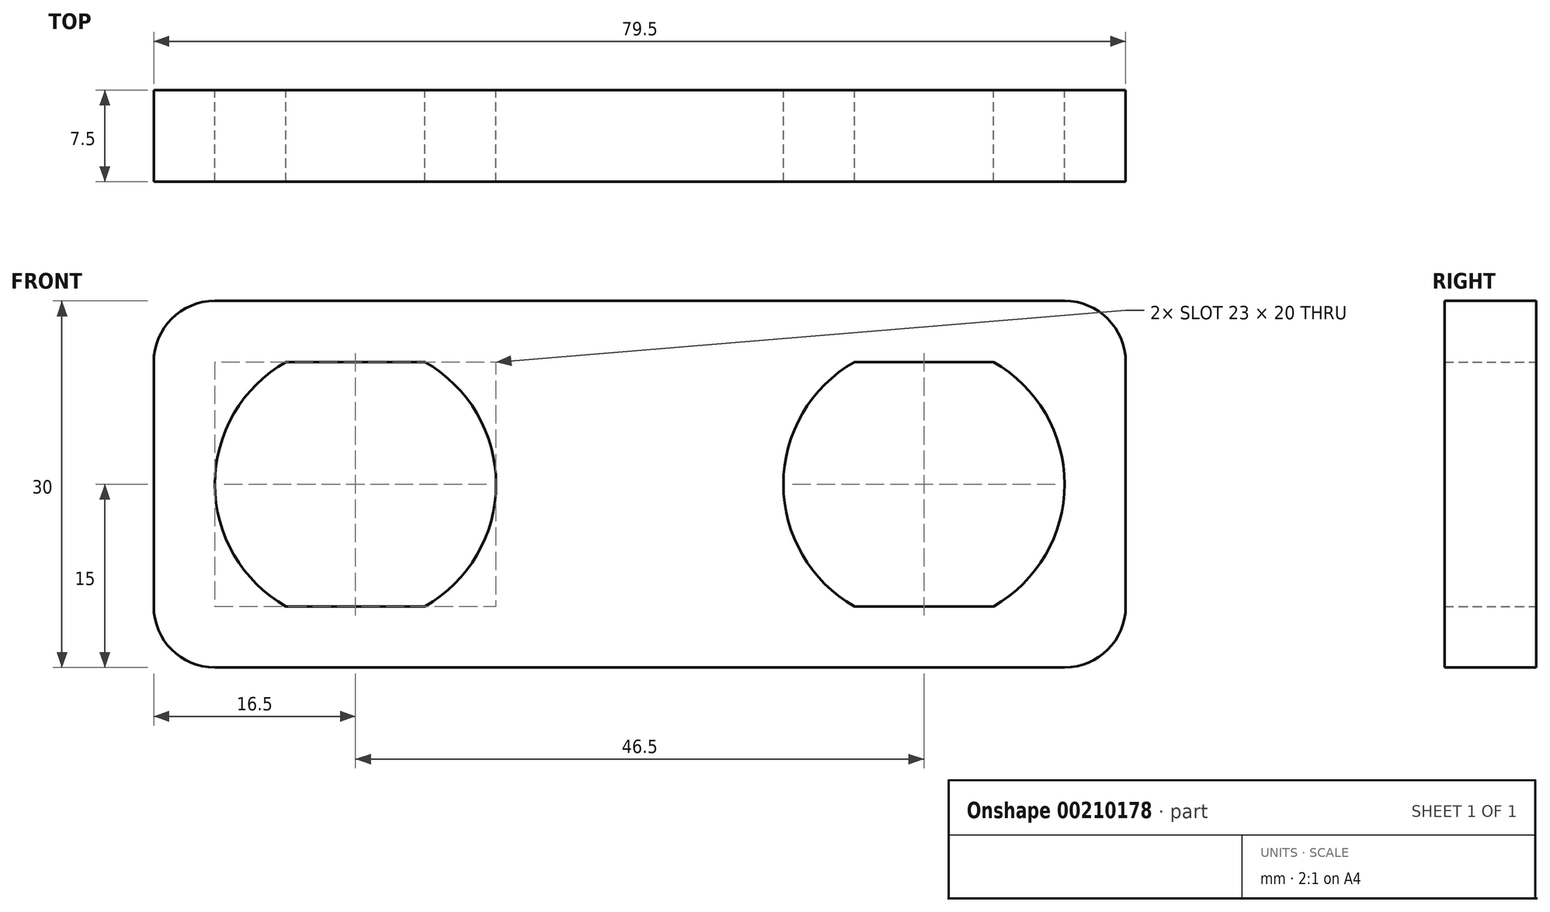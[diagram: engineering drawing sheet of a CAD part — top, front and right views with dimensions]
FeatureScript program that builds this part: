
annotation { "Feature Type Name" : "Feature", "Feature Type Description" : "" }
export const myFeature = defineFeature(function(context is Context, id is Id, definition is map)
    precondition{}
    {
        {
            var Q0;
            Q0=qCreatedBy(makeId("Front.planeOp"),FACE);
            var sketch = newSketch(context, id + "F0", { "sketchPlane" : qUnion([Q0])});
            skLineSegment(sketch, "E0", {"start": v(0, 0) * mm, "end": v(-46.5, 0) * mm});
            skCircle(sketch, "E1", {"center": v(-46.5, 0) * mm, "radius": 11.5 * mm});
            skCircle(sketch, "E2", {"center": v(0, 0) * mm, "radius": 11.5 * mm});
            skLineSegment(sketch, "E3", {"start": v(-35, 0) * mm, "end": v(-11.5, 0) * mm});
            skLineSegment(sketch, "E4", {"start": v(-46.5, 0) * mm, "end": v(-46.5, 10) * mm});
            skLineSegment(sketch, "E5", {"start": v(-46.5, 0) * mm, "end": v(-46.5, -10) * mm});
            skLineSegment(sketch, "E6", {"start": v(-46.5, 10) * mm, "end": v(-40.82, 10) * mm});
            skLineSegment(sketch, "E7", {"start": v(5.68, -10) * mm, "end": v(-5.68, -10) * mm});
            skLineSegment(sketch, "E8.trimOffspring", {"start": v(-5.68, 10) * mm, "end": v(5.68, 10) * mm});
            skLineSegment(sketch, "E9.trimOffspring", {"start": v(-40.82, -10) * mm, "end": v(-52.18, -10) * mm});
            skLineSegment(sketch, "E10", {"start": v(-46.5, 10) * mm, "end": v(-52.18, 10) * mm});
            skLineSegment(sketch, "E11", {"start": v(-58, 0) * mm, "end": v(-63, 0) * mm});
            skLineSegment(sketch, "E12", {"start": v(-63, 0) * mm, "end": v(-63, 15) * mm});
            skLineSegment(sketch, "E13", {"start": v(11.5, 0) * mm, "end": v(16.5, 0) * mm});
            skLineSegment(sketch, "E14", {"start": v(16.5, 0) * mm, "end": v(16.5, 15) * mm});
            skLineSegment(sketch, "E15", {"start": v(16.5, 15) * mm, "end": v(-63, 15) * mm});
            skLineSegment(sketch, "E16.MirrorCS", {"start": v(16.5, 0) * mm, "end": v(16.5, -15) * mm});
            skLineSegment(sketch, "E17.MirrorCS", {"start": v(16.5, -15) * mm, "end": v(-63, -15) * mm});
            skLineSegment(sketch, "E18.MirrorCS", {"start": v(-63, 0) * mm, "end": v(-63, -15) * mm});
            skText(sketch, "E19", { "text": "259", "fontName": "OpenSans-Regular.ttf"});
            const initialGuessF0  = {"E19": [-0.03467, 0.00376, 1, 0, 0.0096]};
            skSetInitialGuess(sketch, initialGuessF0);
            skSolve(sketch);
        }
        {
            var Q0;
            Q0 = qSketchRegion(id + "F0", true);
            var Q1;
            Q1=makeQuery(id+"F0.imprint","IMPRINT",FACE,{"disambiguationData":[TD([[makeQuery(id+"F0.imprint","IMPRINT",EDGE,{"derivedFrom":sQuery(id+"F0.wireOp",EDGE,"E19.sketch_text.stroke-55")}),1.0]])]});
            var Q2;
            Q2=makeQuery(id+"F0.imprint","IMPRINT",FACE,{"disambiguationData":[TD([[makeQuery(id+"F0.imprint","IMPRINT",EDGE,{"derivedFrom":sQuery(id+"F0.wireOp",EDGE,"E19.sketch_text.stroke-39")}),-1.0]])]});
            var Q3;
            Q3=makeQuery(id+"F0.imprint","IMPRINT",FACE,{"disambiguationData":[TD([[makeQuery(id+"F0.imprint","IMPRINT",EDGE,{"derivedFrom":sQuery(id+"F0.wireOp",EDGE,"E19.sketch_text.stroke-20")}),-1.0]])]});
            var Q4;
            Q4=makeQuery(id+"F0.imprint","IMPRINT",FACE,{"disambiguationData":[TD([[makeQuery(id+"F0.imprint","IMPRINT",EDGE,{"derivedFrom":sQuery(id+"F0.wireOp",EDGE,"E19.sketch_text.stroke-0")}),-1.0]])]});
            var Q5;
            {var subQ0=sQuery(id+"F0.wireOp",EDGE,"E8.trimOffspring");Q5=makeQuery(id+"F0.imprint","IMPRINT",FACE,{"disambiguationData":[TD([[makeQuery(id+"F0.imprint","IMPRINT",EDGE,{"derivedFrom":subQ0}),1.0]])]});}
            var Q6;
            {var subQ0=sQuery(id+"F0.wireOp",EDGE,"E7");Q6=makeQuery(id+"F0.imprint","IMPRINT",FACE,{"disambiguationData":[TD([[makeQuery(id+"F0.imprint","IMPRINT",EDGE,{"derivedFrom":subQ0}),1.0]])]});}
            var Q7;
            {var subQ0=sQuery(id+"F0.wireOp",EDGE,"E9.trimOffspring");var subQ1=sQuery(id+"F0.wireOp",EDGE,"E1");var subQ2=makeQuery(id+"F0.imprint","INTERSECT",VERTEX,{"disambiguationData":[OD(0.0)],"derivedFrom":[subQ1,subQ0]});Q7=makeQuery(id+"F0.imprint","IMPRINT",FACE,{"disambiguationData":[TD([[makeQuery(id+"F0.imprint","IMPRINT",EDGE,{"disambiguationData":[TD([[subQ2,1.0]])],"derivedFrom":subQ1}),1.0]])]});}
            var Q8;
            {var subQ0=sQuery(id+"F0.wireOp",EDGE,"E6");Q8=makeQuery(id+"F0.imprint","IMPRINT",FACE,{"disambiguationData":[TD([[makeQuery(id+"F0.imprint","IMPRINT",EDGE,{"derivedFrom":subQ0}),1.0]])]});}
            extrude(context, id + "F1", {"entities" : qUnion([Q0, Q1, Q2, Q3, Q4, Q5, Q6, Q7, Q8]), "depth" : 7.5 * mm});
        }
        {
            var Q0;
            Q0=makeQuery(id+"F1.opExtrude","SWEPT_EDGE",EDGE,{"disambiguationData":[OSD([sQuery(id+"F0.wireOp",EDGE,"E17.MirrorCS"),sQuery(id+"F0.wireOp",EDGE,"E18.MirrorCS")])]});
            var Q1;
            Q1=makeQuery(id+"F1.opExtrude","SWEPT_EDGE",EDGE,{"disambiguationData":[OSD([sQuery(id+"F0.wireOp",EDGE,"E12"),sQuery(id+"F0.wireOp",EDGE,"E15")])]});
            var Q2;
            Q2=makeQuery(id+"F1.opExtrude","SWEPT_EDGE",EDGE,{"disambiguationData":[OSD([sQuery(id+"F0.wireOp",EDGE,"E16.MirrorCS"),sQuery(id+"F0.wireOp",EDGE,"E17.MirrorCS")])]});
            var Q3;
            Q3=makeQuery(id+"F1.opExtrude","SWEPT_EDGE",EDGE,{"disambiguationData":[OSD([sQuery(id+"F0.wireOp",EDGE,"E14"),sQuery(id+"F0.wireOp",EDGE,"E15")])]});
            fillet(context, id + "F2", {"entities" : qUnion([Q0, Q1, Q2, Q3]), "radius" : 5 * mm, "tangentPropagation" : true, "allowEdgeOverflow" : false});
        }
    });
